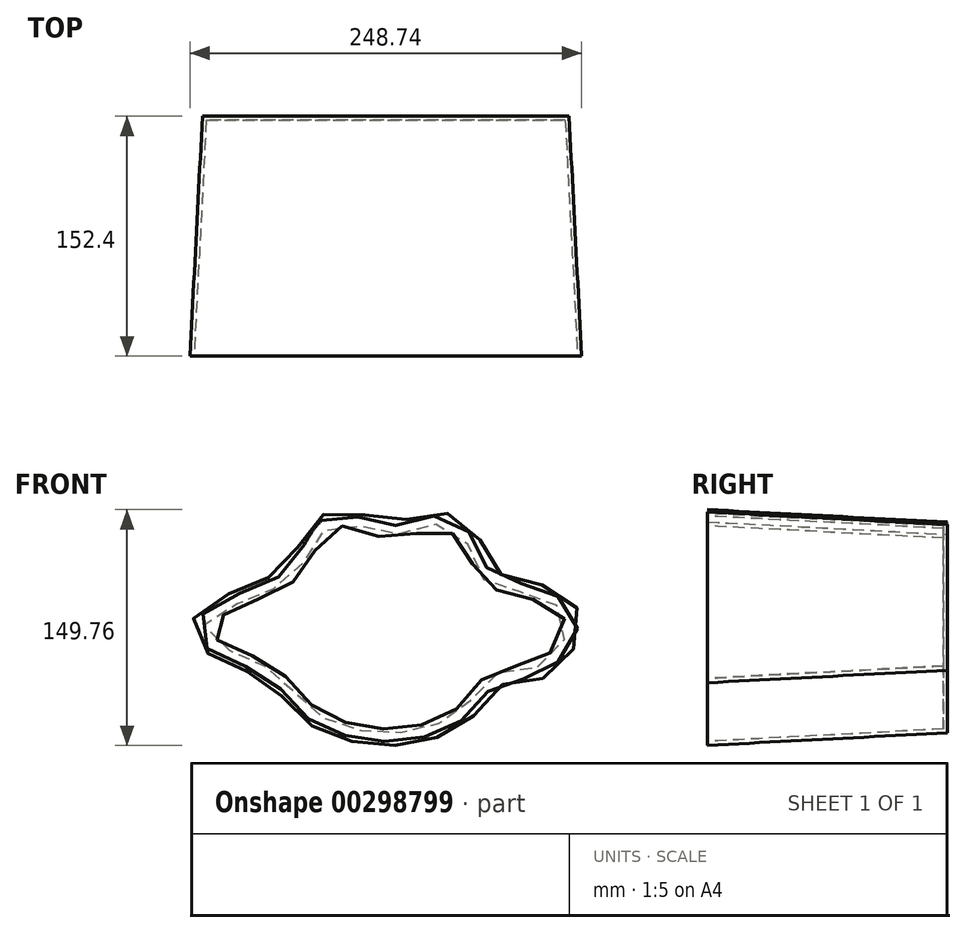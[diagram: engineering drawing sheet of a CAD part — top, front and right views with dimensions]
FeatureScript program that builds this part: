
annotation { "Feature Type Name" : "Feature", "Feature Type Description" : "" }
export const myFeature = defineFeature(function(context is Context, id is Id, definition is map)
    precondition{}
    {
        {
            var Q0;
            Q0=qCreatedBy(makeId("Front.planeOp"),FACE);
            var sketch = newSketch(context, id + "F0", { "sketchPlane" : qUnion([Q0])});
            skPoint(sketch, "E0.middle", {"position": v(0, 0) * mm});
            skPoint(sketch, "E1.17.internal.snap0", {"position": v(76.2, 0) * mm});
            skFitSpline(sketch, "E1", {"points": [v(-76.2, 25.4) * mm, v(-62.88, 33.42) * mm, v(-50.8, 50.8) * mm, v(-34.6, 68.15) * mm, v(0, 60.59) * mm, v(30.92, 66.75) * mm, v(50.8, 50.8) * mm, v(57.8, 33.14) * mm, v(76.2, 25.4) * mm, v(112.69, 6.54) * mm, v(93.09, -23.7) * mm, v(76.2, -25.4) * mm, v(60.6, -32.1) * mm, v(44.92, -50.8) * mm, v(0, -65.42) * mm, v(-50.8, -50.8) * mm, v(-76.2, -25.4) * mm, v(-119.73, 0) * mm, v(-76.2, 25.4) * mm]});
            skSolve(sketch);
        }
        {
            var Q0;
            Q0=makeQuery(id+"F0.imprint","IMPRINT",FACE,{"disambiguationData":[TD([[makeQuery(id+"F0.imprint","IMPRINT",EDGE,{"derivedFrom":sQuery(id+"F0.wireOp",EDGE,"E1")}),-1.0]])]});
            extrude(context, id + "F1", {"entities" : qUnion([Q0]), "depth" : 152.4 * mm, "hasDraft" : true, "draftAngle" : 3 * degree});
        }
        {
            var Q0;
            Q0=makeQuery(id+"F1.opExtrude","CAP_FACE",FACE,{"disambiguationData":[OSD([sQuery(id+"F0.wireOp",EDGE,"E1")])],"isStart":false});
            shell(context, id + "F2", {"entities" : qUnion([Q0]), "thickness" : 2.54 * mm});
        }
    });
